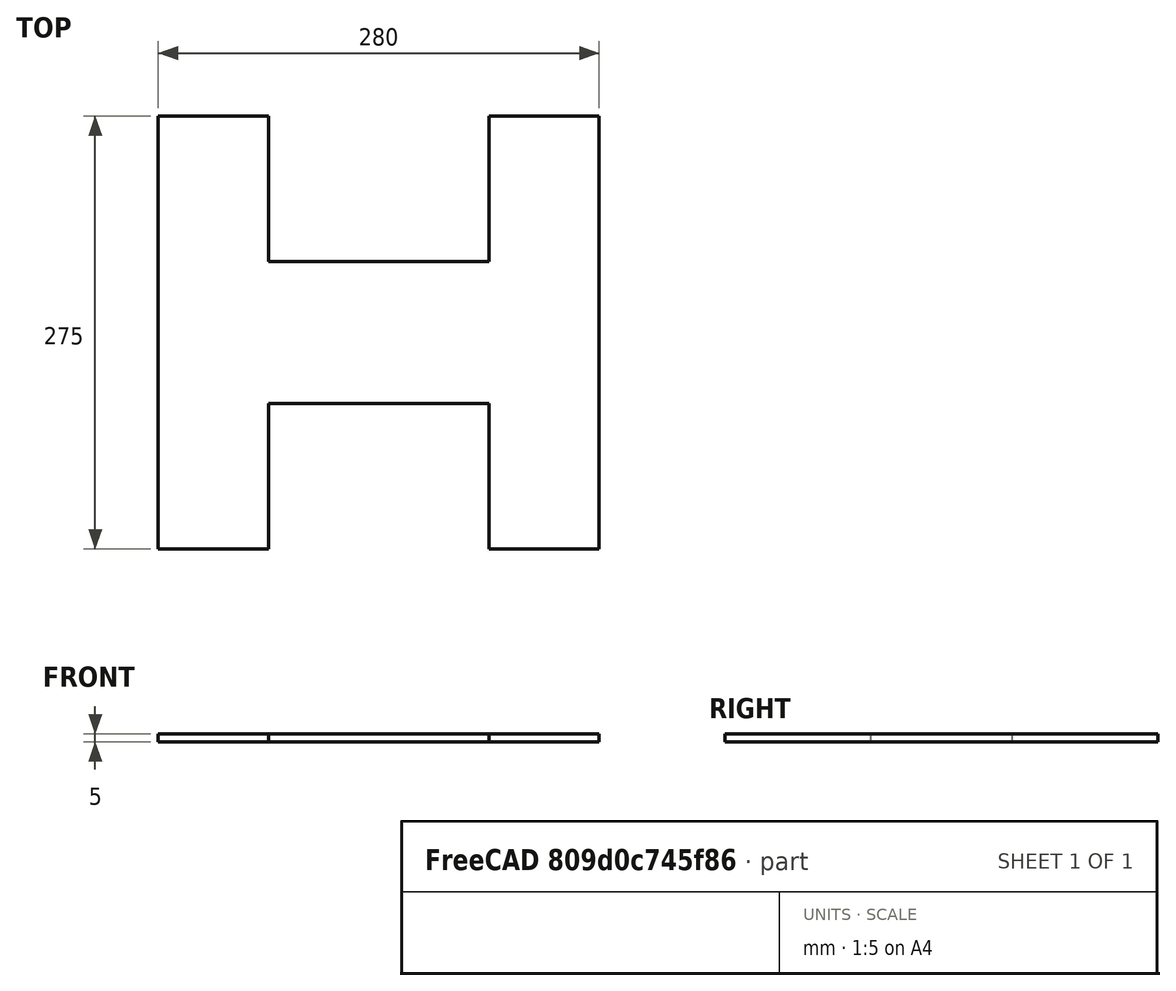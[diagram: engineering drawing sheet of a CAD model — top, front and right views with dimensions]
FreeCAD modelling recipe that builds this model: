
FCSTD DOCUMENT  (FreeCAD 0.15R4671 (Git))
Label: frame_base_0
License: All rights reserved
LicenseURL: http://en.wikipedia.org/wiki/All_rights_reserved
objects: Drawing::FeatureViewPart×3, Sketcher::SketchObject×1, PartDesign::Pad×1, Drawing::FeaturePage×1
note: 3 computed .brp shape members not serialized (recipe doc carries the construction recipe); baked Part::Feature solids carry a one-line shape summary decoded from their .brp

FEATURE [Sketcher::SketchObject] Sketch
  sketch-geometry (12):
    g0: LineSegment StartX=-140 StartY=137.5 StartZ=0 EndX=-70 EndY=137.5 EndZ=0
    g1: LineSegment StartX=-70 StartY=137.5 StartZ=0 EndX=-70 EndY=45 EndZ=0
    g2: LineSegment StartX=-70 StartY=45 StartZ=0 EndX=70 EndY=45 EndZ=0
    g3: LineSegment StartX=70 StartY=45 StartZ=0 EndX=70 EndY=137.5 EndZ=0
    g4: LineSegment StartX=70 StartY=137.5 StartZ=0 EndX=140 EndY=137.5 EndZ=0
    g5: LineSegment StartX=140 StartY=137.5 StartZ=0 EndX=140 EndY=-137.5 EndZ=0
    g6: LineSegment StartX=140 StartY=-137.5 StartZ=0 EndX=70 EndY=-137.5 EndZ=0
    g7: LineSegment StartX=70 StartY=-137.5 StartZ=0 EndX=70 EndY=-45 EndZ=0
    g8: LineSegment StartX=70 StartY=-45 StartZ=0 EndX=-70 EndY=-45 EndZ=0
    g9: LineSegment StartX=-70 StartY=-45 StartZ=0 EndX=-70 EndY=-137.5 EndZ=0
    g10: LineSegment StartX=-70 StartY=-137.5 StartZ=0 EndX=-140 EndY=-137.5 EndZ=0
    g11: LineSegment StartX=-140 StartY=-137.5 StartZ=0 EndX=-140 EndY=137.5 EndZ=0
  constraints (37):
    c: Horizontal(g0)
    c: Coincident(g0,g1)
    c: Vertical(g1)
    c: Coincident(g1,g2)
    c: Horizontal(g2)
    c: Coincident(g2,g3)
    c: Vertical(g3)
    c: Coincident(g3,g4)
    c: Horizontal(g4)
    c: Coincident(g4,g5)
    c: Vertical(g5)
    c: Coincident(g5,g6)
    c: Horizontal(g6)
    c: Coincident(g6,g7)
    c: Vertical(g7)
    c: Coincident(g7,g8)
    c: Horizontal(g8)
    c: Coincident(g8,g9)
    c: Vertical(g9)
    c: Coincident(g9,g10)
    c: Horizontal(g10)
    c: Coincident(g10,g11)
    c: Coincident(g11,g0)
    c: Vertical(g11)
    c: Equal(g11,g5)
    c: Equal(g3,g1)
    c: Equal(g9,g7)
    c: Equal(g0,g10)
    c: Equal(g4,g6)
    c: DistanceY(g11) = 275
    c: Symmetric(g10,g0,g-1)
    c: Symmetric(g7,g2,g-1)
    c: DistanceX(g10,g5) = 280
    c: Equal(g4,g0)
    c: DistanceX(g0) = 70
    c: DistanceY(g1,g8) = -90
    c: Symmetric(g4,g0,g-2)
FEATURE [PartDesign::Pad] Pad
  Length = 5
  Length2 = 100
  Midplane = true
  Sketch = -> Sketch
  Type = 0
FEATURE [Drawing::FeatureViewPart] Ortho  label="Ortho_0_0"
  Direction = (1,0,0)
  HiddenWidth = 0.15
  LineWidth = 0.35
  Rotation = -90
  Scale = 0.375
  ShowHiddenLines = false
  ShowSmoothLines = false
  Source = -> Pad
  Tolerance = 0.05
  ViewResult = <g id="Ortho_0_0"\n   transform="rotate(-90,91.1875,147.354) translate(91.1875,147.354) scale(0.375,0.375)"\n  >\n<g   stroke="rgb(0, 0, 0)"\n   stroke-width="0.933333"\n   stroke-linecap="butt"\n   stroke-linejoin="miter"\n   fill="none"\n   transform="scale(1,-1)"\n  >\n<path id= "1" d=" M -2.5 -137.5 L 2.5 -137.5 " />\n<path id= "2" d=" M -2.5 137.5 L 2.5 137.5 " />\n<path id= "3" d=" M -2.5 -137.5 L -2.5 137.5 " />\n<path id= "4" d=" M 2.5 -137.5 L 2.5 137.5 " />\n<path id= "5" d=" M -2.5 137.5 L 2.5 137.5 " />\n</g>\n</g>
  Visible = true
  X = 91.1875
  Y = 147.354
FEATURE [Drawing::FeatureViewPart] Ortho001  label="Ortho_0_1"
  Direction = (0,0,1)
  HiddenWidth = 0.15
  LineWidth = 0.35
  Rotation = 90
  Scale = 0.375
  ShowHiddenLines = false
  ShowSmoothLines = false
  Source = -> Pad
  Tolerance = 0.05
  ViewResult = <g id="Ortho_0_1"\n   transform="rotate(90,91.1875,78.2083) translate(91.1875,78.2083) scale(0.375,0.375)"\n  >\n<g   stroke="rgb(0, 0, 0)"\n   stroke-width="0.933333"\n   stroke-linecap="butt"\n   stroke-linejoin="miter"\n   fill="none"\n   transform="scale(1,-1)"\n  >\n<path id= "1" d=" M -140 137.5 L -70 137.5 " />\n<path id= "2" d=" M -70 137.5 L -70 45 " />\n<path id= "3" d=" M -70 45 L 70 45 " />\n<path id= "4" d=" M 70 45 L 70 137.5 " />\n<path id= "5" d=" M 70 137.5 L 140 137.5 " />\n<path id= "6" d=" M 140 137.5 L 140 -137.5 " />\n<path id= "7" d=" M 140 -137.5 L 70 -137.5 " />\n<path id= "8" d=" M 70 -137.5 L 70 -45 " />\n<path id= "9" d=" M 70 -45 L -70 -45 " />\n<path id= "10" d=" M -70 -45 L -70 -137.5 " />\n<path id= "11" d=" M -70 -137.5 L -140 -137.5 " />\n<path id= "12" d=" M -140 -137.5 L -140 137.5 " />\n</g>\n</g>
  Visible = true
  X = 91.1875
  Y = 78.2083
FEATURE [Drawing::FeatureViewPart] Ortho002  label="Ortho_1_1"
  Direction = (0.57735,0.57735,0.57735)
  HiddenWidth = 0.15
  LineWidth = 0.35
  Rotation = 120
  Scale = 0.375
  ShowHiddenLines = false
  ShowSmoothLines = false
  Source = -> Pad
  Tolerance = 0.05
  ViewResult = <g id="Ortho_1_1"\n   transform="rotate(120,214.875,78.2083) translate(214.875,78.2083) scale(0.375,0.375)"\n  >\n<g   stroke="rgb(0, 0, 0)"\n   stroke-width="0.933333"\n   stroke-linecap="butt"\n   stroke-linejoin="miter"\n   fill="none"\n   transform="scale(1,-1)"\n  >\n<path id= "1" d=" M -97.2272 170.444 L -100.763 168.402 " />\n<path id= "2" d=" M -47.7297 141.866 L -51.2652 139.825 " />\n<path id= "3" d=" M -97.2272 170.444 L -47.7297 141.866 " />\n<path id= "4" d=" M -100.763 168.402 L -51.2652 139.825 " />\n<path id= "5" d=" M -47.7297 66.3403 L -51.2652 64.2991 " />\n<path id= "6" d=" M -47.7297 141.866 L -47.7297 66.3403 " />\n<path id= "7" d=" M -51.2652 139.825 L -51.2652 64.2991 " />\n<path id= "8" d=" M -47.7297 66.3403 L 47.7297 11.2268 " />\n<path id= "9" d=" M -51.2652 64.2991 L 47.7297 7.14435 " />\n<path id= "10" d=" M 51.2652 84.7115 L 47.7297 82.6703 " />\n<path id= "11" d=" M 47.7297 7.14435 L 47.7297 82.6703 " />\n<path id= "12" d=" M 100.763 56.1341 L 97.2272 54.0929 " />\n<path id= "13" d=" M 51.2652 84.7115 L 100.763 56.1341 " />\n<path id= "14" d=" M 47.7297 82.6703 L 97.2272 54.0929 " />\n<path id= "15" d=" M 100.763 -168.402 L 97.2272 -170.444 " />\n<path id= "16" d=" M 100.763 56.1341 L 100.763 -168.402 " />\n<path id= "17" d=" M 97.2272 54.0929 L 97.2272 -170.444 " />\n<path id= "18" d=" M 97.2272 -170.444 L 47.7297 -141.866 " />\n<path id= "19" d=" M 47.7297 -141.866 L 47.7297 -66.3403 " />\n<path id= "20" d=" M 47.7297 -66.3403 L -51.2652 -9.18559 " />\n<path id= "21" d=" M -47.7297 -82.6703 L -51.2652 -84.7115 " />\n<path id= "22" d=" M -47.7297 -11.2268 L -47.7297 -82.6703 " />\n<path id= "23" d=" M -51.2652 -9.18559 L -51.2652 -84.7115 " />\n<path id= "24" d=" M -51.2652 -84.7115 L -100.763 -56.1341 " />\n<path id= "25" d=" M -100.763 -56.1341 L -100.763 168.402 " />\n</g>\n</g>
  Visible = true
  X = 214.875
  Y = 78.2083
FEATURE [Drawing::FeaturePage] Page
  EditableTexts = Siqueira | Tuane | Pindí | Drawing | Frame | 0022 | 2015-06-21
  Group = -> [Ortho,Ortho001,Ortho002]
  Template = <path>
note: 1 file-system path scrubbed to <path> (originals preserved in the JSON sidecar)
